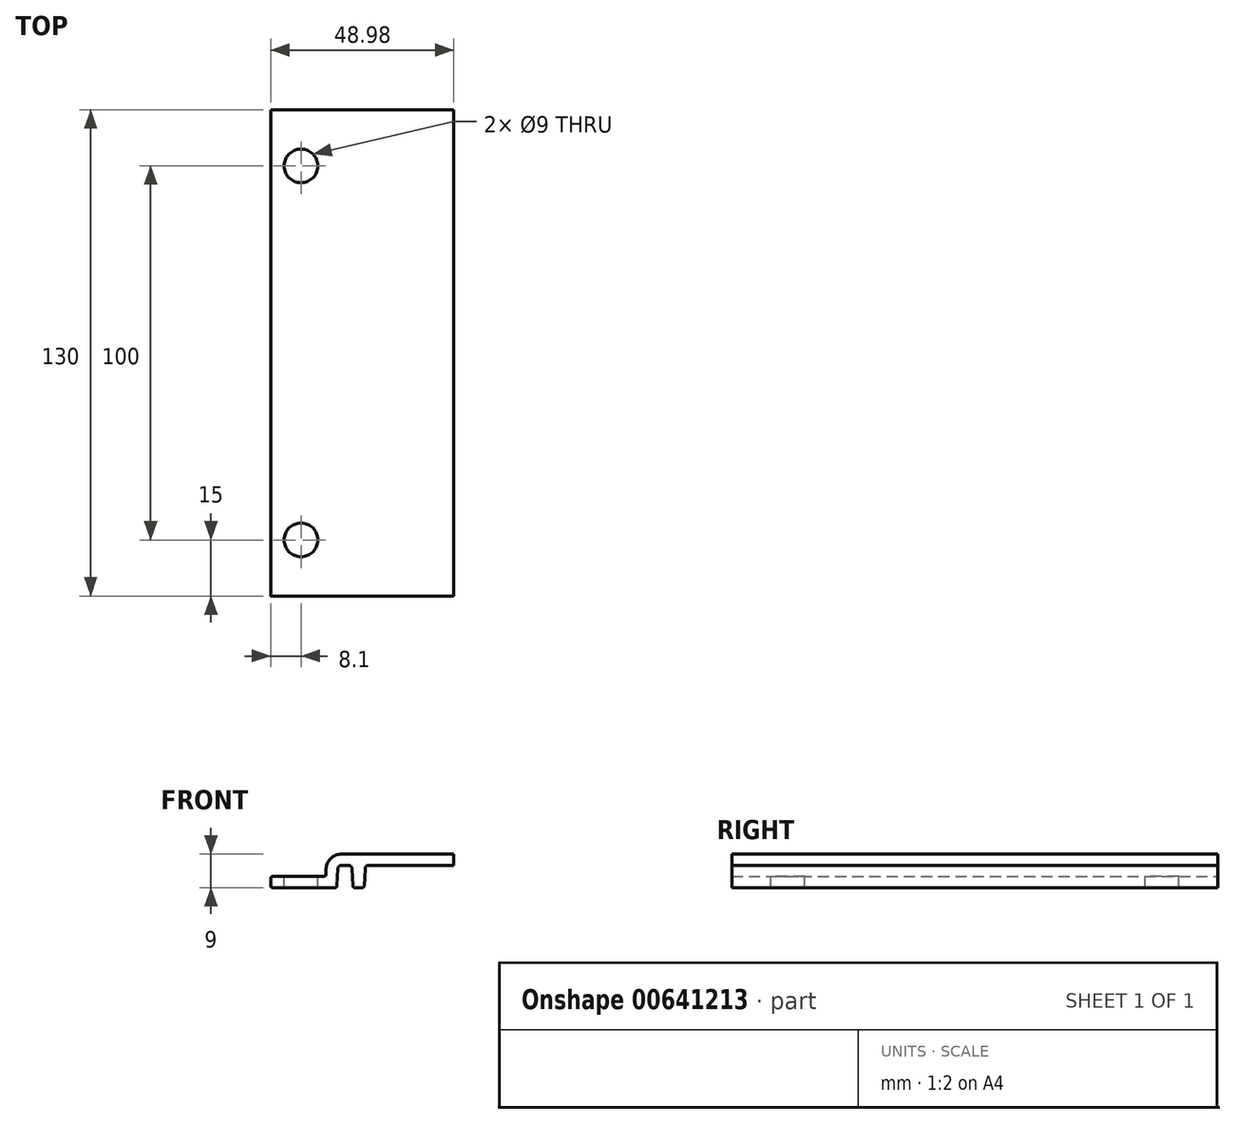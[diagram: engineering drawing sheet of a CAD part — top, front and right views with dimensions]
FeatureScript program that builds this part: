
annotation { "Feature Type Name" : "Feature", "Feature Type Description" : "" }
export const myFeature = defineFeature(function(context is Context, id is Id, definition is map)
    precondition{}
    {
        {
            var Q0;
            Q0=qCreatedBy(makeId("Front.planeOp"),FACE);
            var sketch = newSketch(context, id + "F0", { "sketchPlane" : qUnion([Q0])});
            skLineSegment(sketch, "E0", {"start": v(18.98, 9) * mm, "end": v(48.98, 9) * mm});
            skLineSegment(sketch, "E1", {"start": v(48.98, 9) * mm, "end": v(48.98, 6) * mm});
            skLineSegment(sketch, "E2", {"start": v(48.98, 6) * mm, "end": v(26.24, 6) * mm});
            skArc(sketch, "E3", {"start": v(26.24, 6) * mm, "mid": v(25.55, 5.73) * mm, "end": v(25.24, 5.05) * mm});
            skLineSegment(sketch, "E4", {"start": v(25.24, 5.05) * mm, "end": v(25, 0.47) * mm});
            skArc(sketch, "E5", {"start": v(24.5, 0) * mm, "mid": v(24.84, 0.14) * mm, "end": v(25, 0.47) * mm});
            skLineSegment(sketch, "E6", {"start": v(24.5, 0) * mm, "end": v(22.48, 0) * mm});
            skArc(sketch, "E7", {"start": v(21.98, 0.47) * mm, "mid": v(22.14, 0.14) * mm, "end": v(22.48, 0) * mm});
            skLineSegment(sketch, "E8", {"start": v(21.98, 0.47) * mm, "end": v(21.74, 5.05) * mm});
            skArc(sketch, "E9", {"start": v(21.74, 5.05) * mm, "mid": v(21.43, 5.73) * mm, "end": v(20.74, 6) * mm});
            skLineSegment(sketch, "E10", {"start": v(20.74, 6) * mm, "end": v(18.98, 6) * mm});
            skArc(sketch, "E11", {"start": v(18.98, 6) * mm, "mid": v(18.3, 5.73) * mm, "end": v(17.98, 5.05) * mm});
            skLineSegment(sketch, "E12", {"start": v(17.98, 5.05) * mm, "end": v(17.74, 0.47) * mm});
            skArc(sketch, "E13", {"start": v(17.24, 0) * mm, "mid": v(17.58, 0.14) * mm, "end": v(17.74, 0.47) * mm});
            skLineSegment(sketch, "E14", {"start": v(17.24, 0) * mm, "end": v(0.5, 0) * mm});
            skArc(sketch, "E15", {"start": v(18.98, 9) * mm, "mid": v(16.11, 7.86) * mm, "end": v(14.82, 5.05) * mm});
            skLineSegment(sketch, "E16", {"start": v(14.82, 5.05) * mm, "end": v(14.74, 3.47) * mm});
            skArc(sketch, "E17", {"start": v(14.24, 3) * mm, "mid": v(14.58, 3.14) * mm, "end": v(14.74, 3.47) * mm});
            skLineSegment(sketch, "E18", {"start": v(14.24, 3) * mm, "end": v(0.5, 3) * mm});
            skArc(sketch, "E19", {"start": v(0.5, 3) * mm, "mid": v(0.15, 2.85) * mm, "end": v(0, 2.5) * mm});
            skLineSegment(sketch, "E20", {"start": v(0, 2.5) * mm, "end": v(0, 0.5) * mm});
            skArc(sketch, "E21", {"start": v(0, 0.5) * mm, "mid": v(0.15, 0.15) * mm, "end": v(0.5, 0) * mm});
            skLineSegment(sketch, "E22", {"start": v(20.74, 6) * mm, "end": v(26.24, 6) * mm, "construction": true});
            skLineSegment(sketch, "E23", {"start": v(0.5, 3) * mm, "end": v(0.5, 0) * mm, "construction": true});
            skLineSegment(sketch, "E24", {"start": v(18.98, 6) * mm, "end": v(18.98, 9) * mm, "construction": true});
            skLineSegment(sketch, "E25", {"start": v(17.98, 5.05) * mm, "end": v(14.82, 5.05) * mm, "construction": true});
            skSolve(sketch);
        }
        {
            var Q0;
            Q0=qSketchRegion(id+"F0",true);
            extrude(context, id + "F1", {"entities" : qUnion([Q0]), "depth" : 130 * mm, "offsetDistance" : 25 * mm});
        }
        {
            var Q0;
            Q0=makeQuery(id+"F1.opExtrude","SWEPT_FACE",FACE,{"disambiguationData":[OSD([sQuery(id+"F0.wireOp",EDGE,"E18")])]});
            var sketch = newSketch(context, id + "F2", { "sketchPlane" : qUnion([Q0])});
            skLineSegment(sketch, "E26", {"start": v(14.24, -50.18) * mm, "end": v(0.5, -50.18) * mm, "construction": true});
            skPoint(sketch, "E27", {"position": v(8.1, -15) * mm});
            skPoint(sketch, "E28", {"position": v(8.1, -115) * mm});
            skLineSegment(sketch, "E29", {"start": v(8.1, -15) * mm, "end": v(8.1, -115) * mm, "construction": true});
            skLineSegment(sketch, "E30", {"start": v(8.1, -15) * mm, "end": v(0.5, -15) * mm, "construction": true});
            skSolve(sketch);
        }
        {
            var Q0;
            Q0=sQuery(id+"F2.wireOp",VERTEX,"E27");
            var Q1;
            Q1=makeQuery(id+"F1.opExtrude","SWEPT_BODY",BODY,{"disambiguationData":[OSD([sQuery(id+"F0.wireOp",EDGE,"E0"),sQuery(id+"F0.wireOp",EDGE,"E1"),sQuery(id+"F0.wireOp",EDGE,"E2"),sQuery(id+"F0.wireOp",EDGE,"E3"),sQuery(id+"F0.wireOp",EDGE,"E4"),sQuery(id+"F0.wireOp",EDGE,"E5"),sQuery(id+"F0.wireOp",EDGE,"E6"),sQuery(id+"F0.wireOp",EDGE,"E7"),sQuery(id+"F0.wireOp",EDGE,"E8"),sQuery(id+"F0.wireOp",EDGE,"E9"),sQuery(id+"F0.wireOp",EDGE,"E10"),sQuery(id+"F0.wireOp",EDGE,"E11"),sQuery(id+"F0.wireOp",EDGE,"E12"),sQuery(id+"F0.wireOp",EDGE,"E13"),sQuery(id+"F0.wireOp",EDGE,"E14"),sQuery(id+"F0.wireOp",EDGE,"E15"),sQuery(id+"F0.wireOp",EDGE,"E16"),sQuery(id+"F0.wireOp",EDGE,"E17"),sQuery(id+"F0.wireOp",EDGE,"E18"),sQuery(id+"F0.wireOp",EDGE,"E19"),sQuery(id+"F0.wireOp",EDGE,"E20"),sQuery(id+"F0.wireOp",EDGE,"E21")])]});
            hole(context, id + "F3", {"style" : HoleStyle.SIMPLE, "endStyle" : HoleEndStyle.THROUGH, "holeDiameter" : 9 * mm, "majorDiameter" : 5 * mm, "isTappedThrough" : true, "tappedDepth" : 12 * mm, "tapClearance" : 3, "locations" : qUnion([Q0]), "scope" : qUnion([Q1])});
        }
        {
            var Q0;
            Q0=sQuery(id+"F2.wireOp",VERTEX,"E28");
            var Q1;
            Q1=makeQuery(id+"F1.opExtrude","SWEPT_BODY",BODY,{"disambiguationData":[OSD([sQuery(id+"F0.wireOp",EDGE,"E0"),sQuery(id+"F0.wireOp",EDGE,"E1"),sQuery(id+"F0.wireOp",EDGE,"E2"),sQuery(id+"F0.wireOp",EDGE,"E3"),sQuery(id+"F0.wireOp",EDGE,"E4"),sQuery(id+"F0.wireOp",EDGE,"E5"),sQuery(id+"F0.wireOp",EDGE,"E6"),sQuery(id+"F0.wireOp",EDGE,"E7"),sQuery(id+"F0.wireOp",EDGE,"E8"),sQuery(id+"F0.wireOp",EDGE,"E9"),sQuery(id+"F0.wireOp",EDGE,"E10"),sQuery(id+"F0.wireOp",EDGE,"E11"),sQuery(id+"F0.wireOp",EDGE,"E12"),sQuery(id+"F0.wireOp",EDGE,"E13"),sQuery(id+"F0.wireOp",EDGE,"E14"),sQuery(id+"F0.wireOp",EDGE,"E15"),sQuery(id+"F0.wireOp",EDGE,"E16"),sQuery(id+"F0.wireOp",EDGE,"E17"),sQuery(id+"F0.wireOp",EDGE,"E18"),sQuery(id+"F0.wireOp",EDGE,"E19"),sQuery(id+"F0.wireOp",EDGE,"E20"),sQuery(id+"F0.wireOp",EDGE,"E21")])]});
            hole(context, id + "F4", {"style" : HoleStyle.SIMPLE, "endStyle" : HoleEndStyle.THROUGH, "holeDiameter" : 9 * mm, "majorDiameter" : 5 * mm, "isTappedThrough" : true, "tappedDepth" : 12 * mm, "tapClearance" : 3, "locations" : qUnion([Q0]), "scope" : qUnion([Q1])});
        }
    });
